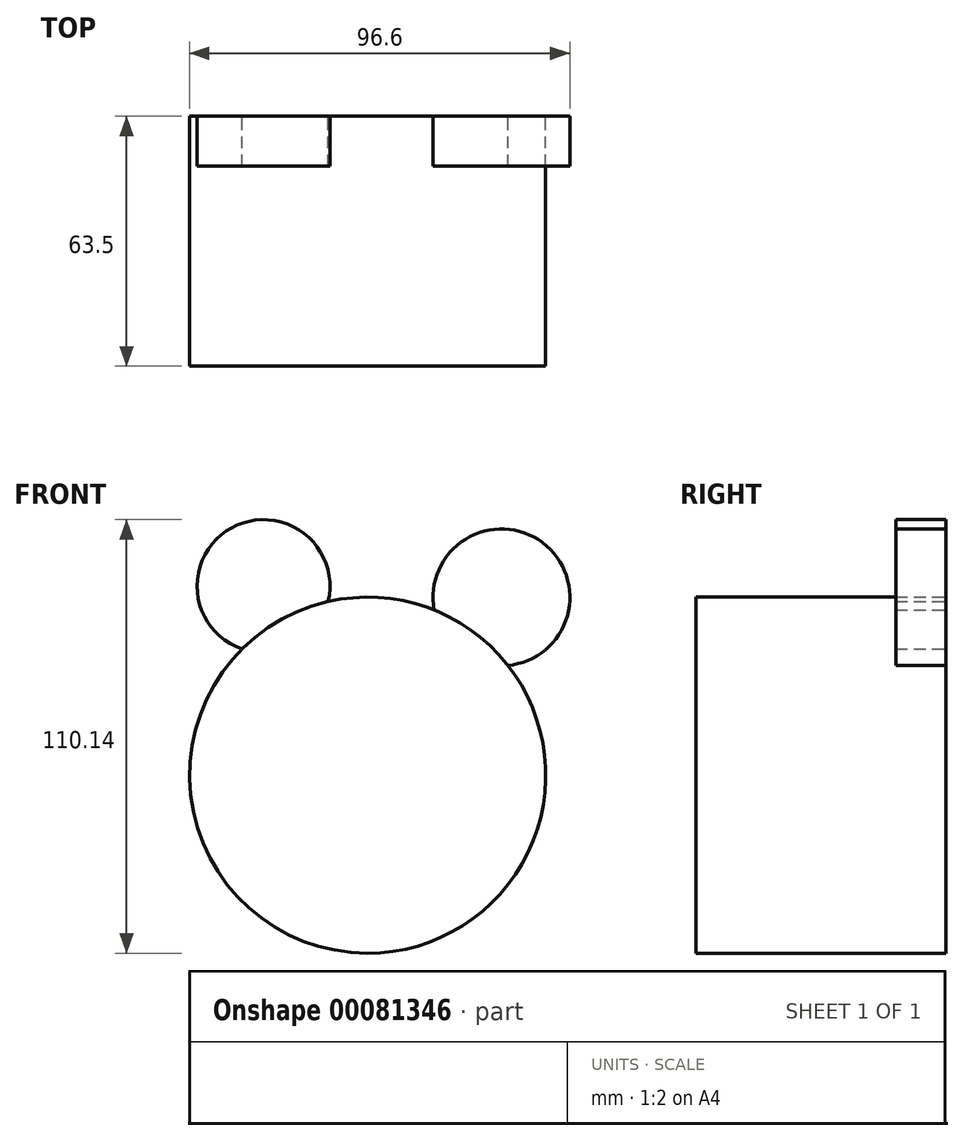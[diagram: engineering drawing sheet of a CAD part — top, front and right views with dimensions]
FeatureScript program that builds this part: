
annotation { "Feature Type Name" : "Feature", "Feature Type Description" : "" }
export const myFeature = defineFeature(function(context is Context, id is Id, definition is map)
    precondition{}
    {
        {
            var Q0;
            Q0=qCreatedBy(makeId("Front.planeOp"),FACE);
            var sketch = newSketch(context, id + "F0", { "sketchPlane" : qUnion([Q0])});
            skCircle(sketch, "E0", {"center": v(0, 0) * mm, "radius": 45.23 * mm});
            skSolve(sketch);
        }
        {
            var Q0;
            Q0=makeQuery(id+"F0.imprint","IMPRINT",FACE,{"disambiguationData":[TD([[makeQuery(id+"F0.imprint","IMPRINT",EDGE,{"derivedFrom":sQuery(id+"F0.wireOp",EDGE,"E0")}),1.0]])]});
            extrude(context, id + "F1", {"entities" : qUnion([Q0]), "depth" : 63.5 * mm});
        }
        {
            var Q0;
            Q0=qCreatedBy(makeId("Front.planeOp"),FACE);
            var sketch = newSketch(context, id + "F2", { "sketchPlane" : qUnion([Q0])});
            skCircle(sketch, "E1", {"center": v(-26.45, 48.03) * mm, "radius": 16.89 * mm});
            skCircle(sketch, "E2", {"center": v(33.98, 45.18) * mm, "radius": 17.38 * mm});
            skSolve(sketch);
        }
        {
            var Q0;
            Q0 = qSketchRegion(id + "F2", true);
            var Q1;
            Q1=makeQuery(id+"F2.imprint","IMPRINT",FACE,{"disambiguationData":[TD([[makeQuery(id+"F2.imprint","IMPRINT",EDGE,{"derivedFrom":sQuery(id+"F2.wireOp",EDGE,"E2")}),1.0]])]});
            extrude(context, id + "F3", {"entities" : qUnion([Q0, Q1]), "operationType" : NewBodyOperationType.ADD, "depth" : 12.7 * mm});
        }
    });
